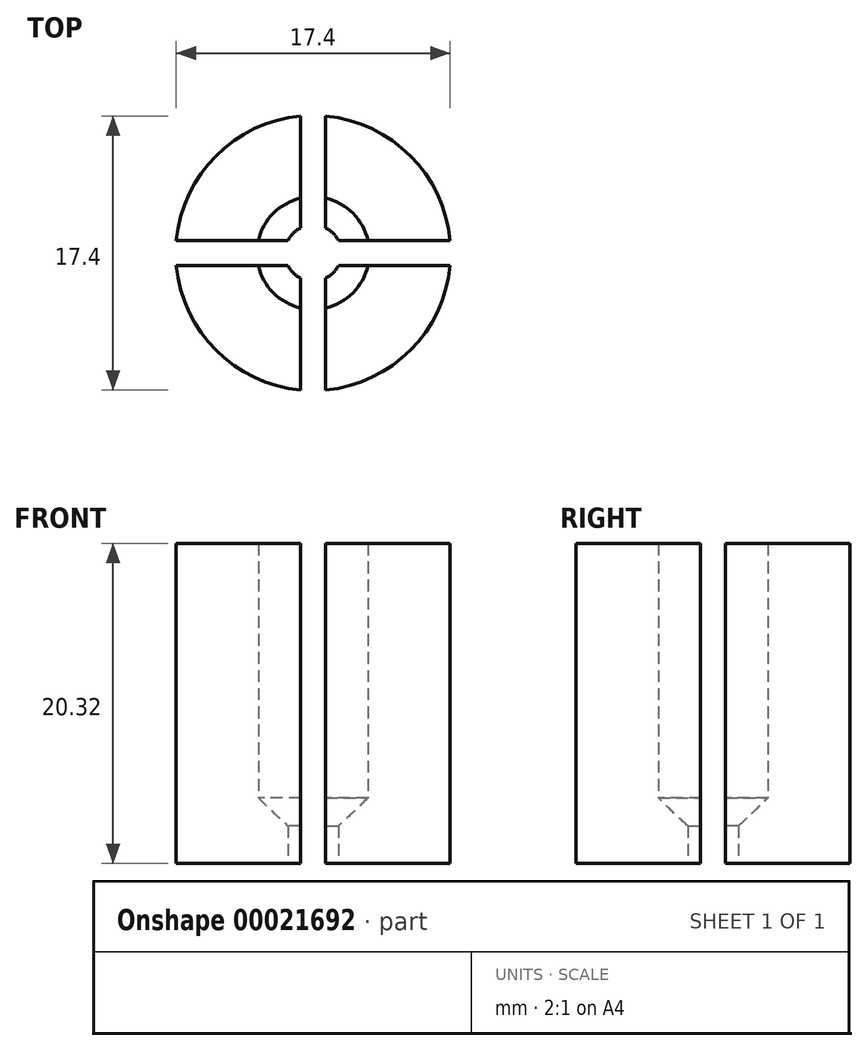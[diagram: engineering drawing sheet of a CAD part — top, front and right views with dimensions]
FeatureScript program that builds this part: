
annotation { "Feature Type Name" : "Feature", "Feature Type Description" : "" }
export const myFeature = defineFeature(function(context is Context, id is Id, definition is map)
    precondition{}
    {
        {
            var Q0;
            Q0=qCreatedBy(makeId("Front.planeOp"),FACE);
            var sketch = newSketch(context, id + "F0", { "sketchPlane" : qUnion([Q0])});
            skLineSegment(sketch, "E0", {"start": v(-12.9, 0) * mm, "end": v(14.67, 0) * mm, "construction": true});
            skLineSegment(sketch, "E1", {"start": v(0, -7.98) * mm, "end": v(0, 8.8) * mm, "construction": true});
            skLineSegment(sketch, "E2", {"start": v(-1.79, 0) * mm, "end": v(-1.79, 2.38) * mm});
            skLineSegment(sketch, "E3", {"start": v(-1.79, 2.38) * mm, "end": v(-3.57, 4.17) * mm});
            skLineSegment(sketch, "E4", {"start": v(-3.57, 4.17) * mm, "end": v(-3.57, 20.32) * mm});
            skLineSegment(sketch, "E5", {"start": v(-3.57, 20.32) * mm, "end": v(-8.73, 20.32) * mm});
            skLineSegment(sketch, "E6", {"start": v(-8.73, 20.32) * mm, "end": v(-8.73, 0) * mm});
            skLineSegment(sketch, "E7", {"start": v(-8.73, 0) * mm, "end": v(-1.79, 0) * mm});
            skSolve(sketch);
        }
        {
            var Q0;
            Q0=makeQuery(id+"F0.imprint","IMPRINT",FACE,{"disambiguationData":[TD([[makeQuery(id+"F0.imprint","IMPRINT",EDGE,{"derivedFrom":sQuery(id+"F0.wireOp",EDGE,"E2")}),1.0]])]});
            var Q1;
            Q1=sQuery(id+"F0.wireOp",EDGE,"E1");
            revolve(context, id + "F1", {"entities" : qUnion([Q0]), "axis" : qUnion([Q1]), "revolveType" : RevolveType.FULL});
        }
        {
            var Q0;
            Q0=makeQuery(id+"F1.opRevolve","SWEPT_FACE",FACE,{"disambiguationData":[OSD([sQuery(id+"F0.wireOp",EDGE,"E5")])]});
            var sketch = newSketch(context, id + "F2", { "sketchPlane" : qUnion([Q0])});
            skLineSegment(sketch, "E8", {"start": v(-0.8, 8.73) * mm, "end": v(0.8, 8.73) * mm});
            skLineSegment(sketch, "E9", {"start": v(0.8, 8.73) * mm, "end": v(0.8, 0.8) * mm});
            skLineSegment(sketch, "E10", {"start": v(0.8, 0.8) * mm, "end": v(8.73, 0.8) * mm});
            skLineSegment(sketch, "E11", {"start": v(8.73, 0.8) * mm, "end": v(8.73, -0.8) * mm});
            skLineSegment(sketch, "E12", {"start": v(8.73, -0.8) * mm, "end": v(0.8, -0.8) * mm});
            skLineSegment(sketch, "E13", {"start": v(0.8, -0.8) * mm, "end": v(0.8, -8.73) * mm});
            skLineSegment(sketch, "E14", {"start": v(0.8, -8.73) * mm, "end": v(-0.8, -8.73) * mm});
            skLineSegment(sketch, "E15", {"start": v(-0.8, -8.73) * mm, "end": v(-0.8, -0.8) * mm});
            skLineSegment(sketch, "E16", {"start": v(-0.8, -0.8) * mm, "end": v(-8.73, -0.8) * mm});
            skLineSegment(sketch, "E17", {"start": v(-8.73, -0.8) * mm, "end": v(-8.73, 0.8) * mm});
            skLineSegment(sketch, "E18", {"start": v(-8.73, 0.8) * mm, "end": v(-0.8, 0.8) * mm});
            skLineSegment(sketch, "E19", {"start": v(-0.8, 0.8) * mm, "end": v(-0.8, 8.73) * mm});
            skLineSegment(sketch, "E20", {"start": v(-13.3, 0) * mm, "end": v(17.5, 0) * mm, "construction": true});
            skLineSegment(sketch, "E21", {"start": v(0, -11.74) * mm, "end": v(0, 10.1) * mm, "construction": true});
            skSolve(sketch);
        }
        {
            var Q0;
            Q0 = qSketchRegion(id + "F2", true);
            extrude(context, id + "F3", {"entities" : qUnion([Q0]), "operationType" : NewBodyOperationType.REMOVE, "endBound" : BoundingType.THROUGH_ALL, "oppositeDirection" : true, "depth" : 25.4 * mm});
        }
    });
